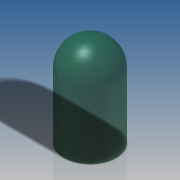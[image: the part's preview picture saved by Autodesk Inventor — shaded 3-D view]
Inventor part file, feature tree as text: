
AUTODESK INVENTOR PART (.ipt)
format: ipt  version: 2016 SP2 (Build 200236200, 236)  size: 109,568 bytes
history: native  units: in
note: dims shown in document units (in); Inventor stores cm internally (conversion verified against a paired STEP export)
features: revolve x1, sketch x1
ambient origin geometry x8: Origin, YZ Plane, XZ Plane, XY Plane, X Axis, Y Axis, Z Axis, Center Point
bodies: Solid1 (feature_tree)
feature tree (2):
  revolve  "Revolution1"  [1 undecoded]
  sketch  "Sketch2"  dims[d0=0.126in d1=0.2205in d2=90.0deg]
note: 1 required parameter value undecoded (feature->parameter linkage not recoverable at this tier; creation-order binding heuristic only, values carry confidence <= 0.55)
